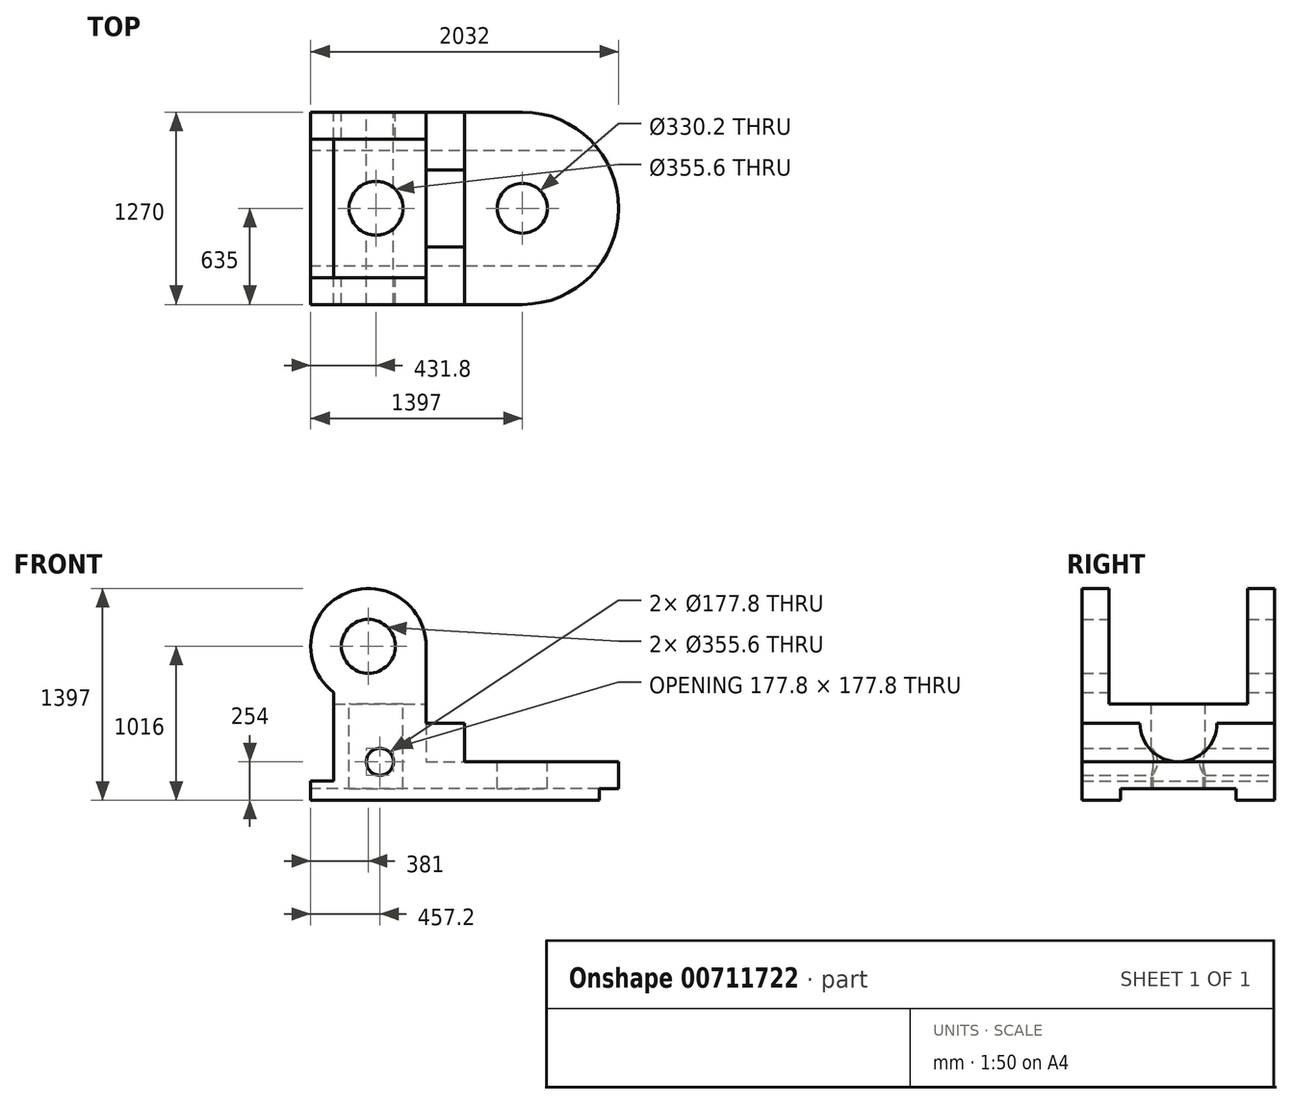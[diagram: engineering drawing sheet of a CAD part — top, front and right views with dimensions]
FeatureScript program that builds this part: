
annotation { "Feature Type Name" : "Feature", "Feature Type Description" : "" }
export const myFeature = defineFeature(function(context is Context, id is Id, definition is map)
    precondition{}
    {
        {
            var Q0;
            Q0=qCreatedBy(makeId("Front.planeOp"),FACE);
            var sketch = newSketch(context, id + "F0", { "sketchPlane" : qUnion([Q0])});
            skLineSegment(sketch, "E0", {"start": v(0, 0) * mm, "end": v(0, 2004.4) * mm, "construction": true});
            skLineSegment(sketch, "E1", {"start": v(0, 0) * mm, "end": v(1984.14, 0) * mm, "construction": true});
            skLineSegment(sketch, "E2", {"start": v(0, 0) * mm, "end": v(1397, 0) * mm});
            skLineSegment(sketch, "E3", {"start": v(1397, 0) * mm, "end": v(1397, 254) * mm});
            skLineSegment(sketch, "E4", {"start": v(1397, 254) * mm, "end": v(762, 254) * mm});
            skLineSegment(sketch, "E5", {"start": v(762, 254) * mm, "end": v(762, 1016) * mm});
            skLineSegment(sketch, "E6", {"start": v(0, 0) * mm, "end": v(0, 127) * mm});
            skLineSegment(sketch, "E7", {"start": v(0, 127) * mm, "end": v(152.4, 127) * mm});
            skLineSegment(sketch, "E8", {"start": v(152.4, 127) * mm, "end": v(152.4, 711.2) * mm});
            skArc(sketch, "E9", {"start": v(762, 1016) * mm, "mid": v(210.61, 1356.78) * mm, "end": v(152.4, 711.2) * mm});
            skCircle(sketch, "E10", {"center": v(381, 1016) * mm, "radius": 177.8 * mm});
            skCircle(sketch, "E11", {"center": v(457.2, 254) * mm, "radius": 88.9 * mm});
            skSolve(sketch);
        }
        {
            var Q0;
            Q0 = qSketchRegion(id + "F0", true);
            extrude(context, id + "F1", {"entities" : qUnion([Q0]), "endBound" : BoundingType.SYMMETRIC, "depth" : 1270 * mm, "offsetDistance" : 25.4 * mm});
        }
        {
            var Q0;
            Q0=makeQuery(id+"F1.opExtrude","SWEPT_FACE",FACE,{"disambiguationData":[OSD([sQuery(id+"F0.wireOp",EDGE,"E4")])]});
            var sketch = newSketch(context, id + "F2", { "sketchPlane" : qUnion([Q0])});
            skLineSegment(sketch, "E12.0", {"start": v(1397, -635) * mm, "end": v(1397, 635) * mm});
            skCircle(sketch, "E13", {"center": v(1397, 0) * mm, "radius": 635 * mm});
            skSolve(sketch);
        }
        {
            var Q0;
            Q0 = qSketchRegion(id + "F2", true);
            extrude(context, id + "F3", {"entities" : qUnion([Q0]), "operationType" : NewBodyOperationType.ADD, "oppositeDirection" : true, "depth" : 254 * mm, "offsetDistance" : 25.4 * mm});
        }
        {
            var Q0;
            Q0=makeQuery(id+"F3.boolean.opBoolean","MERGE",FACE,{"derivedFrom":[makeQuery(id+"F1.opExtrude","SWEPT_FACE",FACE,{"disambiguationData":[OSD([sQuery(id+"F0.wireOp",EDGE,"E4")])]}),makeQuery(id+"F3.opExtrude","CAP_FACE",FACE,{"disambiguationData":[OSD([sQuery(id+"F2.wireOp",EDGE,"E13")])],"isStart":true})]});
            var sketch = newSketch(context, id + "F4", { "sketchPlane" : qUnion([Q0])});
            skArc(sketch, "E14.0", {"start": v(1397, -635) * mm, "mid": v(2032, 0) * mm, "end": v(1397, 635) * mm});
            skCircle(sketch, "E15", {"center": v(1397, 0) * mm, "radius": 165.1 * mm});
            skSolve(sketch);
        }
        {
            var Q0;
            Q0 = qSketchRegion(id + "F4", true);
            extrude(context, id + "F5", {"entities" : qUnion([Q0]), "operationType" : NewBodyOperationType.REMOVE, "endBound" : BoundingType.THROUGH_ALL, "oppositeDirection" : true, "depth" : 25.4 * mm, "offsetDistance" : 25.4 * mm});
        }
        {
            var Q0;
            Q0=makeQuery(id+"F1.opExtrude","SWEPT_FACE",FACE,{"disambiguationData":[OSD([sQuery(id+"F0.wireOp",EDGE,"E5")])]});
            var sketch = newSketch(context, id + "F6", { "sketchPlane" : qUnion([Q0])});
            skLineSegment(sketch, "E16.bottom", {"start": v(-457.2, 1524) * mm, "end": v(457.2, 1524) * mm});
            skLineSegment(sketch, "E16.top", {"start": v(-457.2, 635) * mm, "end": v(457.2, 635) * mm});
            skLineSegment(sketch, "E16.left", {"start": v(-457.2, 1524) * mm, "end": v(-457.2, 635) * mm});
            skLineSegment(sketch, "E16.right", {"start": v(457.2, 1524) * mm, "end": v(457.2, 635) * mm});
            skLineSegment(sketch, "E17", {"start": v(0, 0) * mm, "end": v(0, 1914.7) * mm, "construction": true});
            skPoint(sketch, "E17.endSnap0", {"position": v(0, 254) * mm});
            skSolve(sketch);
        }
        {
            var Q0;
            Q0 = qSketchRegion(id + "F6", true);
            extrude(context, id + "F7", {"entities" : qUnion([Q0]), "operationType" : NewBodyOperationType.REMOVE, "endBound" : BoundingType.THROUGH_ALL, "oppositeDirection" : true, "depth" : 25.4 * mm, "offsetDistance" : 25.4 * mm});
        }
        {
            var Q0;
            Q0=makeQuery(id+"F7.boolean.opBoolean","COPY",FACE,{"derivedFrom":makeQuery(id+"F7.opExtrude","SWEPT_FACE",FACE,{"disambiguationData":[OSD([sQuery(id+"F6.wireOp",EDGE,"E16.top")])]})});
            var sketch = newSketch(context, id + "F8", { "sketchPlane" : qUnion([Q0])});
            skCircle(sketch, "E18", {"center": v(431.8, 0) * mm, "radius": 177.8 * mm});
            skPoint(sketch, "E18.centerSnap0", {"position": v(152.4, 0) * mm});
            skSolve(sketch);
        }
        {
            var Q0;
            Q0 = qSketchRegion(id + "F8", true);
            extrude(context, id + "F9", {"entities" : qUnion([Q0]), "operationType" : NewBodyOperationType.REMOVE, "endBound" : BoundingType.THROUGH_ALL, "oppositeDirection" : true, "depth" : 25.4 * mm, "offsetDistance" : 25.4 * mm});
        }
        {
            var Q0;
            Q0=makeQuery(id+"F1.opExtrude","SWEPT_FACE",FACE,{"disambiguationData":[OSD([sQuery(id+"F0.wireOp",EDGE,"E6")])]});
            var sketch = newSketch(context, id + "F10", { "sketchPlane" : qUnion([Q0])});
            skLineSegment(sketch, "E19.bottom", {"start": v(-381, 0) * mm, "end": v(381, 0) * mm});
            skLineSegment(sketch, "E19.top", {"start": v(-381, 76.2) * mm, "end": v(381, 76.2) * mm});
            skLineSegment(sketch, "E19.left", {"start": v(-381, 0) * mm, "end": v(-381, 76.2) * mm});
            skLineSegment(sketch, "E19.right", {"start": v(381, 0) * mm, "end": v(381, 76.2) * mm});
            skLineSegment(sketch, "E20", {"start": v(0, 0) * mm, "end": v(0, -333.26) * mm, "construction": true});
            skLineSegment(sketch, "E21.0", {"start": v(635, 0) * mm, "end": v(-635, 0) * mm});
            skSolve(sketch);
        }
        {
            var Q0;
            Q0 = qSketchRegion(id + "F10", true);
            extrude(context, id + "F11", {"entities" : qUnion([Q0]), "operationType" : NewBodyOperationType.REMOVE, "endBound" : BoundingType.THROUGH_ALL, "oppositeDirection" : true, "depth" : 25.4 * mm, "offsetDistance" : 25.4 * mm});
        }
        {
            var Q0;
            Q0=makeQuery(id+"F1.opExtrude","SWEPT_FACE",FACE,{"disambiguationData":[OSD([sQuery(id+"F0.wireOp",EDGE,"E5")])]});
            var sketch = newSketch(context, id + "F12", { "sketchPlane" : qUnion([Q0])});
            skLineSegment(sketch, "E22.0", {"start": v(-635, 254) * mm, "end": v(635, 254) * mm});
            skLineSegment(sketch, "E23.top", {"start": v(-635, 508) * mm, "end": v(635, 508) * mm});
            skLineSegment(sketch, "E23.left", {"start": v(-635, 254) * mm, "end": v(-635, 508) * mm});
            skLineSegment(sketch, "E23.right", {"start": v(635, 254) * mm, "end": v(635, 508) * mm});
            skSolve(sketch);
        }
        {
            var Q0;
            Q0 = qSketchRegion(id + "F12", true);
            extrude(context, id + "F13", {"entities" : qUnion([Q0]), "operationType" : NewBodyOperationType.ADD, "depth" : 254 * mm, "offsetDistance" : 25.4 * mm});
        }
        {
            var Q0;
            Q0=makeQuery(id+"F13.opExtrude","CAP_FACE",FACE,{"disambiguationData":[OSD([sQuery(id+"F12.wireOp",EDGE,"E22.0"),sQuery(id+"F12.wireOp",EDGE,"E23.top"),sQuery(id+"F12.wireOp",EDGE,"E23.left"),sQuery(id+"F12.wireOp",EDGE,"E23.right")])],"isStart":false});
            var sketch = newSketch(context, id + "F14", { "sketchPlane" : qUnion([Q0])});
            skLineSegment(sketch, "E24.0", {"start": v(-635, 508) * mm, "end": v(635, 508) * mm});
            skCircle(sketch, "E25", {"center": v(0, 508) * mm, "radius": 254 * mm});
            skSolve(sketch);
        }
        {
            var Q0;
            Q0 = qSketchRegion(id + "F14", true);
            extrude(context, id + "F15", {"entities" : qUnion([Q0]), "operationType" : NewBodyOperationType.REMOVE, "oppositeDirection" : true, "depth" : 254 * mm, "offsetDistance" : 25.4 * mm});
        }
    });
